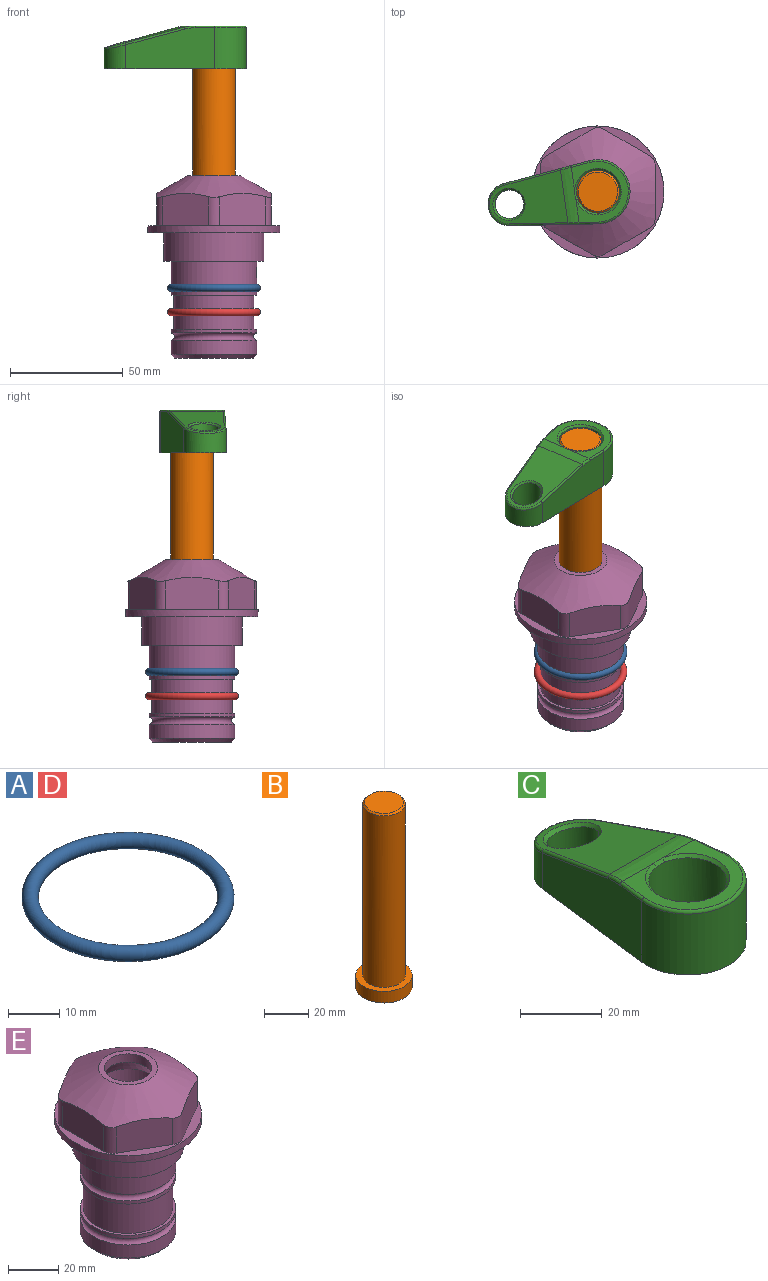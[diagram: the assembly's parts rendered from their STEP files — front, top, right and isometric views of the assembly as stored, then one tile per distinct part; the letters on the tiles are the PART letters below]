
ASSEMBLY  parts=5 mates=4
PART A: 1 faces, bbox 44.7x44.7x3.2 mm
  f0: torus R=19.05mm, axis (0,0,1), area 1193.9mm2
PART B: 6 faces, bbox 25.4x25.4x101.6 mm
  f0: plane 17.46x17.46mm, normal (0,0,1), area 239.5mm2, adj f5
  f1: plane 25.4x25.4mm, normal (0,0,-1), area 506.7mm2, adj f2
  f2: cylinder r=12.7mm len=25.4mm, axis (0,0,1), area 506.7mm2, adj f1,f3
  f3: plane 25.4x25.4mm, normal (0,0,1), area 221.7mm2, adj f2,f4
  f4: cylinder r=9.53mm len=94.46mm, axis (0,0,1), area 5653mm2, adj f3,f5
  f5: cone r=8.73mm half-angle=45deg, axis (0,0,-1), area 64.4mm2, adj f0,f4
PART C: 31 faces, bbox 31.7x65.5x19.8 mm
  f0: plane 39.12x18.26mm, normal (0.99,0.12,0), area 612.2mm2, adj f1,f4,f7,f11,f13,f15
  f1: cylinder r=9.53mm len=18.91mm, axis (0,0,-1), area 296.1mm2, adj f0,f2,f7,f17
  f2: plane 39.12x18.26mm, normal (-0.99,0.12,0), area 612.2mm2, adj f1,f4,f7,f12,f14,f16
  f3: cylinder r=6.35mm len=12.7mm, axis (0,0,-1), area 362.4mm2, adj f7,f18
  f4: cylinder r=14.29mm len=28.58mm, axis (0,0,-1), area 882.2mm2, adj f0,f2,f7,f10
  f5: cylinder r=9.53mm len=19.05mm, axis (0,0,-1), area 1092.6mm2, adj f7,f19,f20
  f6: plane 26.99x23.69mm, normal (0,0,1), area 216.2mm2, adj f9,f10,f11,f12,f19
  f7: plane 63.5x28.58mm, normal (0,0,-1), area 661.8mm2, adj f0,f1,f2,f3,f4,f5,f22,f23
  f8: plane 33.52x23.6mm, normal (0,0.26,0.97), area 486mm2, adj f9,f15,f16,f17,f18
  f9: cylinder r=19.05mm len=24.72mm, axis (1,0,0), area 120.4mm2, adj f6,f8,f13,f14,f20
  f10: torus R=13.49mm, axis (0,0,1), area 59mm2, adj f4,f6,f11,f12
  f11: cylinder r=0.79mm len=8.67mm, axis (0.12,-0.99,0), area 10.8mm2, adj f0,f6,f10,f13
  f12: cylinder r=0.79mm len=8.67mm, axis (0.12,0.99,0), area 10.8mm2, adj f2,f6,f10,f14
  f13: bspline ~4.95x1.42mm, area 6.1mm2, adj f0,f9,f11,f15
  f14: bspline ~4.95x1.42mm, area 6.1mm2, adj f2,f9,f12,f16
  f15: cylinder r=0.79mm len=25.95mm, axis (0.12,-0.96,0.26), area 32.9mm2, adj f0,f8,f13,f17
  f16: cylinder r=0.79mm len=25.95mm, axis (0.12,0.96,-0.26), area 32.9mm2, adj f2,f8,f14,f17
  f17: bspline ~18.91x8.38mm, area 30mm2, adj f1,f8,f15,f16
  f18: bspline ~14.29x14.29mm, area 48.3mm2, adj f3,f8
  f19: cone r=9.53mm half-angle=45deg, axis (0,0,1), area 66.5mm2, adj f5,f6,f20
  f20: bspline ~3.22x0.96mm, area 3.5mm2, adj f5,f9,f19
  f21: plane 2.75x2.72mm, normal (0,0,-1), area 2.9mm2, adj f23,f25,f28
  f22: plane 23.05x15.88mm, normal (-0.99,-0.12,0), area 323.6mm2, adj f7,f25,f26,f27,f28,f29
  f23: plane 23.05x15.88mm, normal (0.99,-0.12,0), area 323.6mm2, adj f7,f21,f25,f27,f28,f30
  f24: cylinder r=9.53mm len=10.69mm, axis (0,0,-1), area 114.7mm2, adj f7,f27,f29,f30
  f25: cylinder r=12.7mm len=20.59mm, axis (0,0,-1), area 381.1mm2, adj f7,f21,f22,f23,f26,f28
  f26: plane 2.75x2.72mm, normal (0,0,-1), area 2.9mm2, adj f22,f25,f28
  f27: plane 19.72x18.37mm, normal (0,-0.26,-0.97), area 291.8mm2, adj f22,f23,f24,f28,f29,f30
  f28: cylinder r=15.88mm len=19.92mm, axis (1,0,0), area 54.8mm2, adj f21,f22,f23,f25,f26,f27
  f29: cylinder r=1.59mm len=11mm, axis (0,0,-1), area 34.7mm2, adj f7,f22,f24,f27
  f30: cylinder r=1.59mm len=11mm, axis (0,0,-1), area 34.7mm2, adj f7,f23,f24,f27
PART D: same geometry as A
PART E: 36 faces, bbox 58.7x58.7x81 mm
  f0: cylinder r=17.78mm len=35.56mm, axis (0,0,1), area 1670.8mm2, adj f23,f24,f31
  f1: cylinder r=19.05mm len=38.1mm, axis (0,0,1), area 1191.9mm2, adj f26,f27,f30
  f2: plane 58.66x58.66mm, normal (0,0,-1), area 1150.6mm2, adj f3,f28
  f3: cylinder r=29.33mm len=58.66mm, axis (0,0,-1), area 585.1mm2, adj f2,f4
  f4: plane 58.66x58.66mm, normal (0,0,1), area 475.9mm2, adj f3,f5,f6,f7,f8,f9,f10,f11
  f5: plane 20.32x14.34mm, normal (-0.5,0.87,0), area 324.4mm2, adj f4,f15,f16,f17
  f6: plane 20.32x14.34mm, normal (0.5,0.87,0), area 324.4mm2, adj f4,f14,f15,f17
  f7: plane 23.48x14.34mm, normal (1,0,0), area 324.4mm2, adj f4,f13,f14,f17
  f8: plane 20.32x14.34mm, normal (0.5,-0.87,0), area 324.4mm2, adj f4,f12,f13,f17
  f9: plane 20.32x14.34mm, normal (-0.5,-0.87,0), area 324.4mm2, adj f4,f11,f12,f17
  f10: plane 23.48x14.34mm, normal (-1,0,0), area 324.4mm2, adj f4,f11,f16,f17
  f11: cylinder r=5.08mm len=12.85mm, axis (0,0,-1), area 67.2mm2, adj f4,f9,f10,f17
  f12: cylinder r=5.08mm len=12.85mm, axis (0,0,-1), area 67.2mm2, adj f4,f8,f9,f17
  f13: cylinder r=5.08mm len=12.85mm, axis (0,0,-1), area 67.2mm2, adj f4,f7,f8,f17
  f14: cylinder r=5.08mm len=12.85mm, axis (0,0,-1), area 67.2mm2, adj f4,f6,f7,f17
  f15: cylinder r=5.08mm len=12.85mm, axis (0,0,-1), area 67.2mm2, adj f4,f5,f6,f17
  f16: cylinder r=5.08mm len=12.85mm, axis (0,0,-1), area 67.2mm2, adj f4,f5,f10,f17
  f17: cone r=11.73mm half-angle=60deg, axis (0,0,-1), area 2071.8mm2, adj f5,f6,f7,f8,f9,f10,f11,f12
  f18: plane 23.46x23.46mm, normal (0,0,1), area 147.4mm2, adj f17,f35
  f19: plane 34.93x34.93mm, normal (0,0,-1), area 958mm2, adj f29
  f20: cylinder r=19.05mm len=38.1mm, axis (0,0,1), area 760.1mm2, adj f21,f29
  f21: torus R=19.05mm, axis (0,0,1), area 565.3mm2, adj f20,f22
  f22: cylinder r=19.05mm len=38.1mm, axis (0,0,1), area 190mm2, adj f21,f23
  f23: plane 38.1x38.1mm, normal (0,0,1), area 146.9mm2, adj f0,f22
  f24: plane 38.1x38.1mm, normal (0,0,-1), area 146.9mm2, adj f0,f25
  f25: cylinder r=19.05mm len=38.1mm, axis (0,0,1), area 190mm2, adj f24,f26
  f26: torus R=19.05mm, axis (0,0,1), area 565.3mm2, adj f1,f25
  f27: plane 44.45x44.45mm, normal (0,0,-1), area 411.7mm2, adj f1,f28
  f28: cylinder r=22.23mm len=44.45mm, axis (0,0,1), area 1773.5mm2, adj f2,f27
  f29: cone r=19.05mm half-angle=45deg, axis (0,0,1), area 257.5mm2, adj f19,f20
  f30: cylinder r=3.17mm len=6.75mm, axis (-1,0,0), area 128mm2, adj f1,f33
  f31: cylinder r=3.17mm len=6.35mm, axis (-1,0,0), area 102.5mm2, adj f0,f33
  f32: plane 25.4x25.4mm, normal (0,0,1), area 506.7mm2, adj f33
  f33: cylinder r=12.7mm len=66.42mm, axis (0,0,-1), area 5236.2mm2, adj f30,f31,f32,f34
  f34: cone r=9.53mm half-angle=30deg, axis (0,0,-1), area 443.4mm2, adj f33,f35
  f35: cylinder r=9.53mm len=19.05mm, axis (0,0,-1), area 240.9mm2, adj f18,f34
PLACE A at identity
PLACE B rot(axis=(0,0,1),98.1deg) t=(0,0,27.55)mm
PLACE C rot(axis=(0,0,1),98.1deg) t=(0,0,28.35)mm
PLACE D t=(0,0,-10.79)mm
PLACE E at identity fixed
MATE fastened D.f0 <-> E.f0  axis (0,0,1) through (0,0,-35.31)mm
MATE fastened A.f0 <-> E.f0  axis (0,0,1) through (0,0,-24.51)mm
MATE fastened C.f4 <-> B.f2  axis (0,0,1) through (0,0,91.05)mm
MATE cylindrical B.f2 <-> E.f0  axis (0,0,-1) through (0,0,-10.55)mm
